# Revit family: Турникет RTD-20
name_source: partatom
category: Обобщенные модели
units: mm (PartAtom-declared; Revit-internal decimal feet)

## family parameters
Всегда вертикально = Да
Может служить основой для арматурных стержней = Нет
На основе рабочей плоскости = Нет
Общий = Нет
При загрузке вырезать с полостями = Нет
Размер круглого соединителя = Использовать диаметр
Тип детали = Нормальный
Точка расчета площади = Нет

## types (4) — shared parameters
ADSK_Единица измерения = компл.
ADSK_Завод-изготовитель = PERCo
ADSK_Количество = 1
ADSK_Масса_Текст = от 370 кг
ADSK_Напряжение = 24В
ADSK_Номинальная мощность = 210Вт
ADSK_Ток = 9А
Габаритыне размеры (длина х ширина х высота) = 1595х2480×2303 мм
Материал турникета = Сталь окрашенная RAL 5010
Подключение к электросети = 220 В
Пропускная способность = 60 чел./мин
Степень защиты оболочки = IP54
Температура использования = от -40°C до +55°C
Ширина зоны прохода = 630 мм
zero-valued in all types: Отметка по умолчанию

## per-type parameters (varying)
| type | ADSK_URL страницы изделия | ADSK_Материал наименование | ADSK_Наименование | ADSK_Наименование краткое | Материал ротора |
| RTD-20.1 Моторизированный | https://www.perco.ru | Корпус и ротор - Сталь, обработанная 
методом горячего цинкования и покрытая порошковой краской. | Сдвоенный полноростовый роторный моторизированный турникет PERCo-RTD-20 | Турникет роторный моторизированный 
сдвоенный RTD-20 | Сталь, окрашенная, белая |
| RTD-20.1S Моторизированный | https://www.perco.ru | Корпус - сталь, обработанная 
методом горячего цинкования и покрытая порошковой краской. 
Ротор - нержавеющая сталь | Сдвоенный полноростовый роторный моторизированный турникет PERCo-RTD-20S | Турникет роторный моторизированный сдвоенный RTD-20S | Сталь, нержавеющая AISI 304 |
| RTD-20.2 Электромеханический | https://www.perco.ru | Корпус и ротор - Сталь, обработанная 
методом горячего цинкования и покрытая порошковой краской. | Сдвоенный полноростовый роторный электромеханичесикй турникет PERCo-RTD-20 | Турникет роторный электромеханичесикй 
сдвоенный RTD-20 | Сталь, окрашенная, белая |
| RTD-20.2S Электромеханичесикй | https://https: | Корпус и ротор - Сталь, обработанная 
методом горячего цинкования и покрытая порошковой краской. | Сдвоенный полноростовый роторный электромеханичесикй турникет PERCo-RTD-20 | Турникет роторный электромеханичесикй 
сдвоенный RTD-20 | Сталь, нержавеющая AISI 304 |
